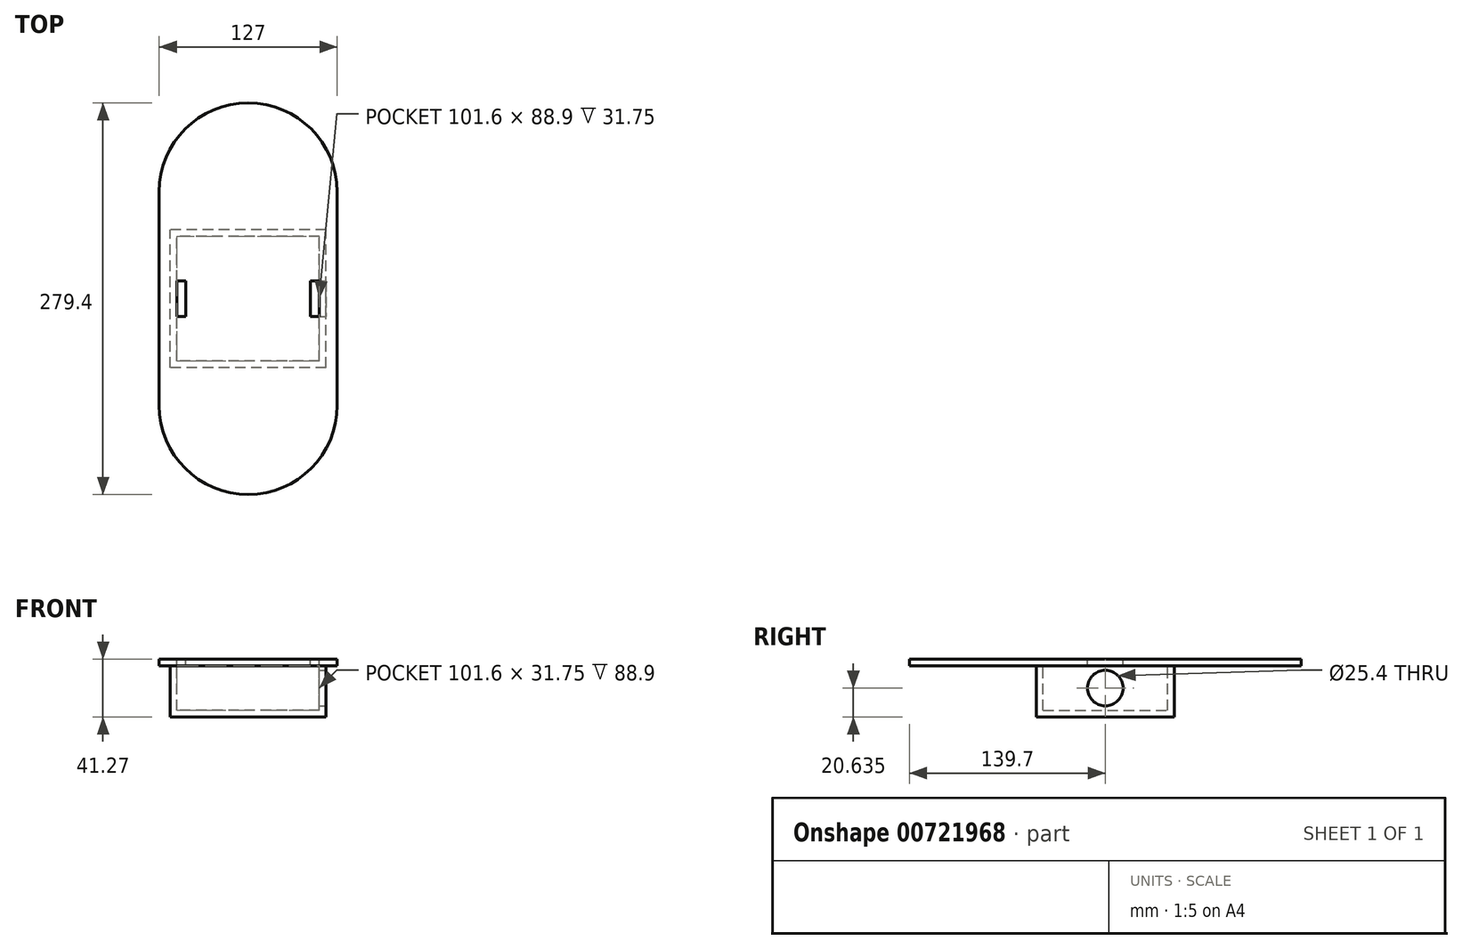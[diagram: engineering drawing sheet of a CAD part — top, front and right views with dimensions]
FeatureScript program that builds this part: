
annotation { "Feature Type Name" : "Feature", "Feature Type Description" : "" }
export const myFeature = defineFeature(function(context is Context, id is Id, definition is map)
    precondition{}
    {
        {
            var Q0;
            Q0=qCreatedBy(makeId("Top.planeOp"),FACE);
            var sketch = newSketch(context, id + "F0", { "sketchPlane" : qUnion([Q0])});
            skLineSegment(sketch, "E0.left", {"start": v(63.5, -76.2) * mm, "end": v(63.5, 76.2) * mm});
            skLineSegment(sketch, "E0.right", {"start": v(-63.5, -76.2) * mm, "end": v(-63.5, 76.2) * mm});
            skPoint(sketch, "E0.middle", {"position": v(0, 0) * mm});
            skArc(sketch, "E1", {"start": v(-63.5, 76.2) * mm, "mid": v(0, 139.7) * mm, "end": v(63.5, 76.2) * mm});
            skArc(sketch, "E2", {"start": v(-63.5, -76.2) * mm, "mid": v(0, -139.7) * mm, "end": v(63.5, -76.2) * mm});
            skSolve(sketch);
        }
        {
            var Q0;
            Q0=makeQuery(id+"F0.imprint","IMPRINT",FACE,{"disambiguationData":[TD([[makeQuery(id+"F0.imprint","IMPRINT",EDGE,{"derivedFrom":sQuery(id+"F0.wireOp",EDGE,"E0.left")}),1.0]])]});
            extrude(context, id + "F1", {"entities" : qUnion([Q0]), "depth" : 4.76 * mm, "offsetDistance" : 25.4 * mm});
        }
        {
            var Q0;
            Q0=makeQuery(id+"F1.opExtrude","CAP_FACE",FACE,{"disambiguationData":[OSD([sQuery(id+"F0.wireOp",EDGE,"E0.left"),sQuery(id+"F0.wireOp",EDGE,"E0.right"),sQuery(id+"F0.wireOp",EDGE,"E1"),sQuery(id+"F0.wireOp",EDGE,"E2")])],"isStart":true});
            var sketch = newSketch(context, id + "F2", { "sketchPlane" : qUnion([Q0])});
            skLineSegment(sketch, "E3.bottom", {"start": v(50.8, 44.45) * mm, "end": v(-50.8, 44.45) * mm});
            skLineSegment(sketch, "E3.top", {"start": v(50.8, -44.45) * mm, "end": v(-50.8, -44.45) * mm});
            skLineSegment(sketch, "E3.left", {"start": v(50.8, 44.45) * mm, "end": v(50.8, -44.45) * mm});
            skLineSegment(sketch, "E3.right", {"start": v(-50.8, 44.45) * mm, "end": v(-50.8, -44.45) * mm});
            skPoint(sketch, "E3.middle", {"position": v(0, 0) * mm});
            skLineSegment(sketch, "E4.0", {"start": v(55.56, 49.21) * mm, "end": v(-55.56, 49.21) * mm});
            skLineSegment(sketch, "E4.1", {"start": v(55.56, 49.21) * mm, "end": v(55.56, -49.21) * mm});
            skLineSegment(sketch, "E4.2", {"start": v(55.56, -49.21) * mm, "end": v(-55.56, -49.21) * mm});
            skLineSegment(sketch, "E4.3", {"start": v(-55.56, 49.21) * mm, "end": v(-55.56, -49.21) * mm});
            skSolve(sketch);
        }
        {
            var Q0;
            Q0=makeQuery(id+"F2.imprint","IMPRINT",FACE,{"disambiguationData":[TD([[makeQuery(id+"F2.imprint","IMPRINT",EDGE,{"derivedFrom":sQuery(id+"F2.wireOp",EDGE,"E3.bottom")}),-1.0]])]});
            extrude(context, id + "F3", {"entities" : qUnion([Q0]), "operationType" : NewBodyOperationType.ADD, "depth" : 31.75 * mm, "offsetDistance" : 25.4 * mm});
        }
        {
            var Q0;
            Q0=makeQuery(id+"F3.opExtrude","SWEPT_FACE",FACE,{"disambiguationData":[OSD([sQuery(id+"F2.wireOp",EDGE,"E4.1")])]});
            var sketch = newSketch(context, id + "F4", { "sketchPlane" : qUnion([Q0])});
            skPoint(sketch, "E5", {"position": v(0, -15.88) * mm});
            skPoint(sketch, "E5.positionSnap0", {"position": v(-49.21, -15.88) * mm});
            skSolve(sketch);
        }
        {
            var Q0;
            Q0=sQuery(id+"F4.wireOp",VERTEX,"E5");
            var Q1;
            Q1=makeQuery(id+"F1.opExtrude","SWEPT_BODY",BODY,{"disambiguationData":[OSD([sQuery(id+"F0.wireOp",EDGE,"E0.left"),sQuery(id+"F0.wireOp",EDGE,"E0.right"),sQuery(id+"F0.wireOp",EDGE,"E1"),sQuery(id+"F0.wireOp",EDGE,"E2")])]});
            hole(context, id + "F5", {"style" : HoleStyle.SIMPLE, "endStyle" : HoleEndStyle.BLIND, "holeDiameter" : 25.4 * mm, "majorDiameter" : 6.35 * mm, "holeDepth" : 50.8 * mm, "isTappedThrough" : true, "tappedDepth" : 12.7 * mm, "tapClearance" : 3, "locations" : qUnion([Q0]), "scope" : qUnion([Q1])});
        }
        {
            var Q0;
            Q0=makeQuery(id+"F1.opExtrude","CAP_FACE",FACE,{"disambiguationData":[OSD([sQuery(id+"F0.wireOp",EDGE,"E0.left"),sQuery(id+"F0.wireOp",EDGE,"E0.right"),sQuery(id+"F0.wireOp",EDGE,"E1"),sQuery(id+"F0.wireOp",EDGE,"E2")])],"isStart":false});
            var sketch = newSketch(context, id + "F6", { "sketchPlane" : qUnion([Q0])});
            skLineSegment(sketch, "E6.bottom", {"start": v(-44.45, -12.7) * mm, "end": v(-50.8, -12.7) * mm});
            skLineSegment(sketch, "E6.top", {"start": v(-44.45, 12.7) * mm, "end": v(-50.8, 12.7) * mm});
            skLineSegment(sketch, "E6.left", {"start": v(-44.45, -12.7) * mm, "end": v(-44.45, 12.7) * mm});
            skLineSegment(sketch, "E6.right", {"start": v(-50.8, -12.7) * mm, "end": v(-50.8, 12.7) * mm});
            skPoint(sketch, "E6.middle", {"position": v(-47.62, 0) * mm});
            skLineSegment(sketch, "E7.bottom", {"start": v(50.8, -12.7) * mm, "end": v(44.45, -12.7) * mm});
            skLineSegment(sketch, "E7.top", {"start": v(50.8, 12.7) * mm, "end": v(44.45, 12.7) * mm});
            skLineSegment(sketch, "E7.left", {"start": v(50.8, -12.7) * mm, "end": v(50.8, 12.7) * mm});
            skLineSegment(sketch, "E7.right", {"start": v(44.45, -12.7) * mm, "end": v(44.45, 12.7) * mm});
            skPoint(sketch, "E7.middle", {"position": v(47.62, 0) * mm});
            skSolve(sketch);
        }
        {
            var Q0;
            Q0=makeQuery(id+"F6.imprint","IMPRINT",FACE,{"disambiguationData":[TD([[makeQuery(id+"F6.imprint","IMPRINT",EDGE,{"derivedFrom":sQuery(id+"F6.wireOp",EDGE,"E7.bottom")}),-1.0]])]});
            var Q1;
            Q1=makeQuery(id+"F6.imprint","IMPRINT",FACE,{"disambiguationData":[TD([[makeQuery(id+"F6.imprint","IMPRINT",EDGE,{"derivedFrom":sQuery(id+"F6.wireOp",EDGE,"E6.bottom")}),-1.0]])]});
            extrude(context, id + "F7", {"entities" : qUnion([Q0, Q1]), "operationType" : NewBodyOperationType.REMOVE, "oppositeDirection" : true, "depth" : 4.76 * mm, "offsetDistance" : 25.4 * mm});
        }
        {
            var Q0;
            Q0=qCreatedBy(makeId("Top.planeOp"),FACE);
            cPlane(context, id + "F8", {"entities" : qUnion([Q0]), "cplaneType" : CPlaneType.OFFSET, "offset" : 31.75 * mm, "oppositeDirection" : true, "width" : 152.4 * mm, "height" : 152.4 * mm});
        }
        {
            var Q0;
            Q0=qCreatedBy(id+"F8.planeOp",FACE);
            var sketch = newSketch(context, id + "F9", { "sketchPlane" : qUnion([Q0])});
            skLineSegment(sketch, "E8.0.0", {"start": v(55.56, -49.21) * mm, "end": v(-55.56, -49.21) * mm});
            skLineSegment(sketch, "E8.0.1", {"start": v(-55.56, -49.21) * mm, "end": v(-55.56, 49.21) * mm});
            skLineSegment(sketch, "E8.0.2", {"start": v(-55.56, 49.21) * mm, "end": v(55.56, 49.21) * mm});
            skLineSegment(sketch, "E8.0.3", {"start": v(55.56, 49.21) * mm, "end": v(55.56, -49.21) * mm});
            skSolve(sketch);
        }
        {
            var Q0;
            Q0=makeQuery(id+"F9.imprint","IMPRINT",FACE,{"disambiguationData":[TD([[makeQuery(id+"F9.imprint","IMPRINT",EDGE,{"derivedFrom":sQuery(id+"F9.wireOp",EDGE,"E8.0.0")}),-1.0]])]});
            extrude(context, id + "F10", {"entities" : qUnion([Q0]), "operationType" : NewBodyOperationType.ADD, "oppositeDirection" : true, "depth" : 4.76 * mm, "offsetDistance" : 25.4 * mm});
        }
    });
